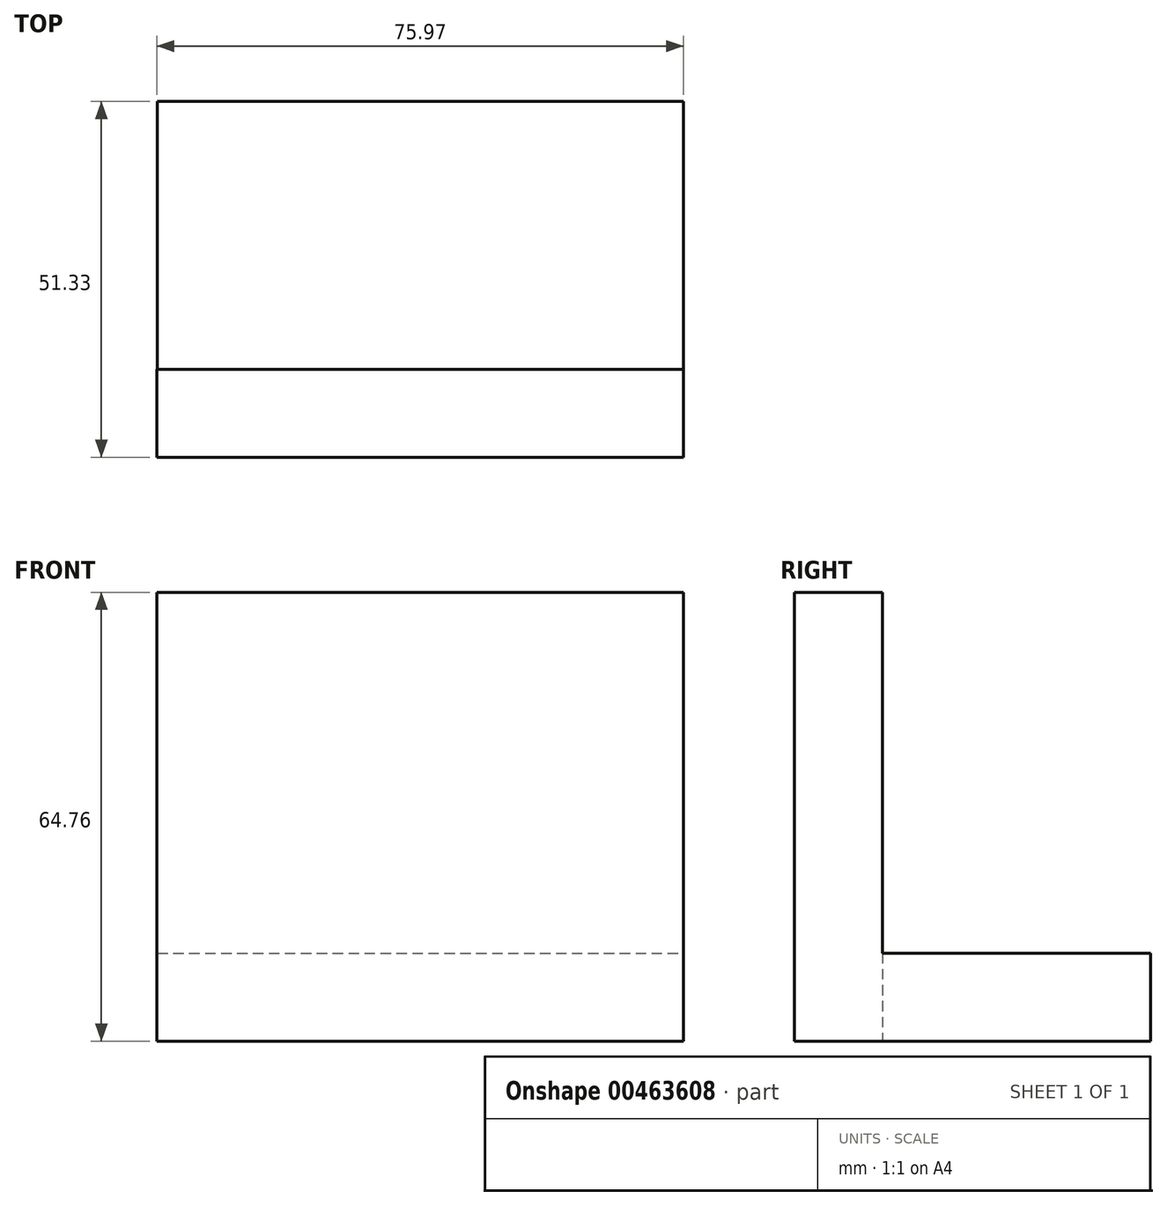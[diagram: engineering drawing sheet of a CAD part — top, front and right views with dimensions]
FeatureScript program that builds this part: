
annotation { "Feature Type Name" : "Feature", "Feature Type Description" : "" }
export const myFeature = defineFeature(function(context is Context, id is Id, definition is map)
    precondition{}
    {
        {
            var Q0;
            Q0=qCreatedBy(makeId("Front.planeOp"),FACE);
            var sketch = newSketch(context, id + "F0", { "sketchPlane" : qUnion([Q0])});
            skLineSegment(sketch, "E0.bottom", {"start": v(-75.97, 64.76) * mm, "end": v(0, 64.76) * mm});
            skLineSegment(sketch, "E0.top", {"start": v(-75.97, 0) * mm, "end": v(0, 0) * mm});
            skLineSegment(sketch, "E0.left", {"start": v(-75.97, 64.76) * mm, "end": v(-75.97, 0) * mm});
            skLineSegment(sketch, "E0.right", {"start": v(0, 64.76) * mm, "end": v(0, 0) * mm});
            skSolve(sketch);
        }
        {
            var Q0;
            Q0 = qSketchRegion(id + "F0", true);
            extrude(context, id + "F1", {"entities" : qUnion([Q0]), "depth" : 12.7 * mm});
        }
        {
            var Q0;
            Q0=qCreatedBy(makeId("Top.planeOp"),FACE);
            var sketch = newSketch(context, id + "F2", { "sketchPlane" : qUnion([Q0])});
            skLineSegment(sketch, "E1.bottom", {"start": v(-75.9, 38.63) * mm, "end": v(0, 38.63) * mm});
            skLineSegment(sketch, "E1.top", {"start": v(-75.9, 0) * mm, "end": v(0, 0) * mm});
            skLineSegment(sketch, "E1.left", {"start": v(-75.9, 38.63) * mm, "end": v(-75.9, 0) * mm});
            skLineSegment(sketch, "E1.right", {"start": v(0, 38.63) * mm, "end": v(0, 0) * mm});
            skSolve(sketch);
        }
        {
            var Q0;
            Q0=makeQuery(id+"F2.imprint","IMPRINT",FACE,{"disambiguationData":[TD([[makeQuery(id+"F2.imprint","IMPRINT",EDGE,{"derivedFrom":sQuery(id+"F2.wireOp",EDGE,"E1.bottom")}),-1.0]])]});
            extrude(context, id + "F3", {"entities" : qUnion([Q0]), "operationType" : NewBodyOperationType.ADD, "depth" : 12.7 * mm});
        }
    });
